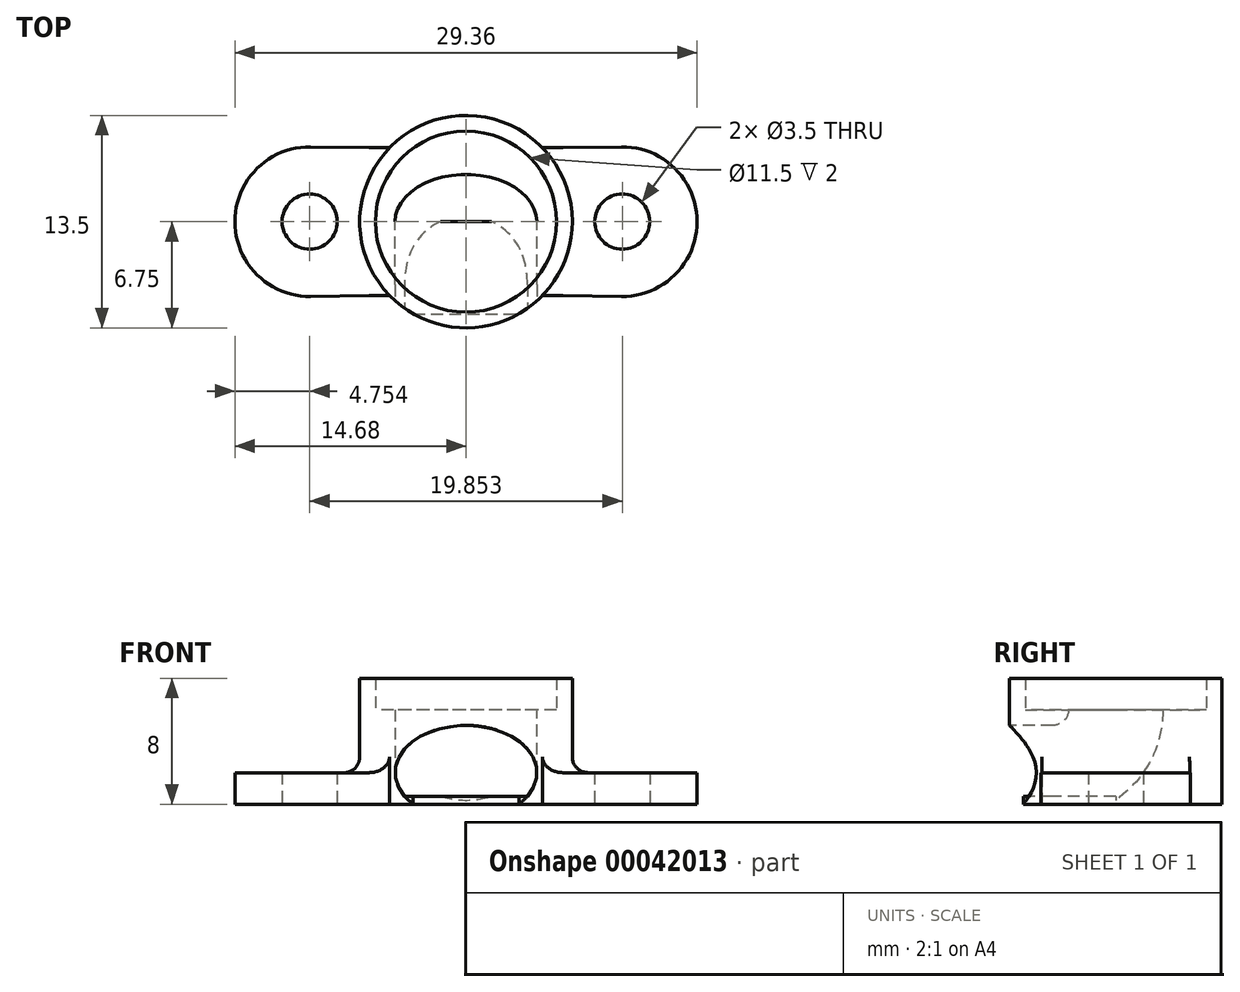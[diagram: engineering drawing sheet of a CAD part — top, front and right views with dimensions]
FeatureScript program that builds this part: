
annotation { "Feature Type Name" : "Feature", "Feature Type Description" : "" }
export const myFeature = defineFeature(function(context is Context, id is Id, definition is map)
    precondition{}
    {
        {
            var Q0;
            Q0=qCreatedBy(makeId("Top.planeOp"),FACE);
            var sketch = newSketch(context, id + "F0", { "sketchPlane" : qUnion([Q0])});
            skCircle(sketch, "E0", {"center": v(0, 0) * mm, "radius": 6.75 * mm});
            skSolve(sketch);
        }
        {
            var Q0;
            Q0=qSketchRegion(id+"F0",true);
            extrude(context, id + "F1", {"entities" : qUnion([Q0]), "depth" : 6 * mm});
        }
        {
            var Q0;
            Q0=makeQuery(id+"F1.opExtrude","CAP_FACE",FACE,{"disambiguationData":[OSD([sQuery(id+"F0.wireOp",EDGE,"E0")])],"isStart":false});
            var sketch = newSketch(context, id + "F2", { "sketchPlane" : qUnion([Q0])});
            skCircle(sketch, "E1", {"center": v(0, 0) * mm, "radius": 5.75 * mm});
            skCircle(sketch, "E2", {"center": v(0, 0) * mm, "radius": 6.75 * mm});
            skSolve(sketch);
        }
        {
            var Q0;
            Q0=makeQuery(id+"F2.imprint","IMPRINT",FACE,{"disambiguationData":[TD([[makeQuery(id+"F2.imprint","IMPRINT",EDGE,{"derivedFrom":sQuery(id+"F2.wireOp",EDGE,"E1")}),-1.0]])]});
            extrude(context, id + "F3", {"entities" : qUnion([Q0]), "operationType" : NewBodyOperationType.ADD, "depth" : 2 * mm});
        }
        {
            var Q0;
            Q0=qCreatedBy(makeId("Top.planeOp"),FACE);
            var sketch = newSketch(context, id + "F4", { "sketchPlane" : qUnion([Q0])});
            skArc(sketch, "E3", {"start": v(-9.87, 4.75) * mm, "mid": v(-14.68, 0) * mm, "end": v(-9.87, -4.75) * mm});
            skLineSegment(sketch, "E4", {"start": v(0, 5.94) * mm, "end": v(0, -6.04) * mm, "construction": true});
            skCircle(sketch, "E5", {"center": v(-9.93, 0) * mm, "radius": 1.75 * mm});
            skArc(sketch, "E6.MirrorCS", {"start": v(9.87, 4.75) * mm, "mid": v(14.68, 0) * mm, "end": v(9.87, -4.75) * mm});
            skCircle(sketch, "E7.MirrorC", {"center": v(9.93, 0) * mm, "radius": 1.75 * mm});
            skLineSegment(sketch, "E8", {"start": v(-5.5, 0) * mm, "end": v(5.77, 0) * mm, "construction": true});
            skLineSegment(sketch, "E9", {"start": v(-9.87, 4.75) * mm, "end": v(-4.85, 4.7) * mm});
            skLineSegment(sketch, "E10", {"start": v(-9.87, -4.75) * mm, "end": v(-4.85, -4.7) * mm});
            skLineSegment(sketch, "E11", {"start": v(9.87, -4.75) * mm, "end": v(4.85, -4.7) * mm});
            skLineSegment(sketch, "E12", {"start": v(9.87, 4.75) * mm, "end": v(4.85, 4.7) * mm});
            skFitSpline(sketch, "E13", {"points": [v(-4.85, -4.7) * mm, v(-4.85, -4.1) * mm, v(-5.7, -2.48) * mm, v(-6.17, 0) * mm, v(-5.5, 2.99) * mm, v(-4.85, 4.7) * mm], "startDerivative": vector(0.89, 4.78) * mm, "endDerivative": vector(3.16, 7.84) * mm});
            skFitSpline(sketch, "E14", {"points": [v(4.85, 4.7) * mm, v(5.63, 2.47) * mm, v(6.24, -0.23) * mm, v(5.72, -2.67) * mm, v(4.85, -4.7) * mm], "startDerivative": vector(3.1, -8.78) * mm, "endDerivative": vector(-3.8, -8.27) * mm});
            skSolve(sketch);
        }
        {
            var Q0;
            Q0=qSketchRegion(id+"F4",true);
            extrude(context, id + "F5", {"entities" : qUnion([Q0]), "operationType" : NewBodyOperationType.ADD, "depth" : 2 * mm});
        }
        {
            var Q0;
            Q0=makeQuery(id+"F5.boolean.opBoolean","INTERSECT",EDGE,{"derivedFrom":[makeQuery(id+"F3.boolean.opBoolean","MERGE",FACE,{"derivedFrom":[makeQuery(id+"F1.opExtrude","SWEPT_FACE",FACE,{"disambiguationData":[OSD([sQuery(id+"F0.wireOp",EDGE,"E0")])]}),makeQuery(id+"F3.opExtrude","SWEPT_FACE",FACE,{"disambiguationData":[OSD([sQuery(id+"F2.wireOp",EDGE,"E2")])]})]}),makeQuery(id+"F5.opExtrude","CAP_FACE",FACE,{"disambiguationData":[OSD([sQuery(id+"F4.wireOp",EDGE,"E6.MirrorCS"),sQuery(id+"F4.wireOp",EDGE,"E7.MirrorC"),sQuery(id+"F4.wireOp",EDGE,"E11"),sQuery(id+"F4.wireOp",EDGE,"E12"),sQuery(id+"F4.wireOp",EDGE,"E14")])],"isStart":false})]});
            var Q1;
            Q1=makeQuery(id+"F5.opExtrude","SWEPT_EDGE",EDGE,{"disambiguationData":[OSD([sQuery(id+"F4.wireOp",EDGE,"E11"),sQuery(id+"F4.wireOp",EDGE,"E14")])]});
            var Q2;
            Q2=makeQuery(id+"F5.opExtrude","SWEPT_EDGE",EDGE,{"disambiguationData":[OSD([sQuery(id+"F4.wireOp",EDGE,"E12"),sQuery(id+"F4.wireOp",EDGE,"E14")])]});
            var Q3;
            Q3=makeQuery(id+"F5.opExtrude","SWEPT_EDGE",EDGE,{"disambiguationData":[OSD([sQuery(id+"F4.wireOp",EDGE,"E9"),sQuery(id+"F4.wireOp",EDGE,"E13")])]});
            var Q4;
            Q4=makeQuery(id+"F5.boolean.opBoolean","INTERSECT",EDGE,{"derivedFrom":[makeQuery(id+"F3.boolean.opBoolean","MERGE",FACE,{"derivedFrom":[makeQuery(id+"F1.opExtrude","SWEPT_FACE",FACE,{"disambiguationData":[OSD([sQuery(id+"F0.wireOp",EDGE,"E0")])]}),makeQuery(id+"F3.opExtrude","SWEPT_FACE",FACE,{"disambiguationData":[OSD([sQuery(id+"F2.wireOp",EDGE,"E2")])]})]}),makeQuery(id+"F5.opExtrude","CAP_FACE",FACE,{"disambiguationData":[OSD([sQuery(id+"F4.wireOp",EDGE,"E3"),sQuery(id+"F4.wireOp",EDGE,"E5"),sQuery(id+"F4.wireOp",EDGE,"E9"),sQuery(id+"F4.wireOp",EDGE,"E10"),sQuery(id+"F4.wireOp",EDGE,"E13")])],"isStart":false})]});
            var Q5;
            Q5=makeQuery(id+"F5.opExtrude","SWEPT_EDGE",EDGE,{"disambiguationData":[OSD([sQuery(id+"F4.wireOp",EDGE,"E10"),sQuery(id+"F4.wireOp",EDGE,"E13")])]});
            fillet(context, id + "F6", {"entities" : qUnion([Q0, Q1, Q2, Q3, Q4, Q5]), "radius" : 1 * mm, "tangentPropagation" : true, "allowEdgeOverflow" : false});
        }
        {
            var Q0;
            Q0=makeQuery(id+"F1.opExtrude","CAP_FACE",FACE,{"disambiguationData":[OSD([sQuery(id+"F0.wireOp",EDGE,"E0")])],"isStart":false});
            var sketch = newSketch(context, id + "F7", { "sketchPlane" : qUnion([Q0])});
            skEllipse(sketch, "E15", {"center": v(0, 0) * mm, "majorRadius": 4.5 * mm, "minorRadius": 3 * mm, "majorAxis": v(1, 0)});
            skSolve(sketch);
        }
        {
            var Q0;
            Q0=qCreatedBy(makeId("Right.planeOp"),FACE);
            var sketch = newSketch(context, id + "F8", { "sketchPlane" : qUnion([Q0])});
            skLineSegment(sketch, "E16", {"start": v(0, 6) * mm, "end": v(0, 6) * mm});
            skLineSegment(sketch, "E17", {"start": v(-4, 2) * mm, "end": v(-9.96, 2) * mm});
            skPoint(sketch, "E18.visualSharp", {"position": v(0, 2) * mm});
            skArc(sketch, "E18.filletArc", {"start": v(-4, 2) * mm, "mid": v(-1.17, 3.17) * mm, "end": v(0, 6) * mm});
            skSolve(sketch);
        }
        {
            var Q0;
            Q0=qSketchRegion(id+"F7",true);
            var Q1;
            Q1=qConstructionFilter(qBodyType(qCreatedBy(id+"F8",EDGE),BodyType.WIRE),ConstructionObject.NO);
            sweep(context, id + "F9", {"operationType" : NewBodyOperationType.REMOVE, "profiles" : qUnion([Q0]), "path" : qUnion([Q1])});
        }
        {
            var Q0;
            Q0=makeQuery(id+"F5.boolean.opBoolean","MERGE",FACE,{"derivedFrom":[makeQuery(id+"F1.opExtrude","CAP_FACE",FACE,{"disambiguationData":[OSD([sQuery(id+"F0.wireOp",EDGE,"E0")])],"isStart":true}),makeQuery(id+"F5.opExtrude","CAP_FACE",FACE,{"disambiguationData":[OSD([sQuery(id+"F4.wireOp",EDGE,"E3"),sQuery(id+"F4.wireOp",EDGE,"E5"),sQuery(id+"F4.wireOp",EDGE,"E9"),sQuery(id+"F4.wireOp",EDGE,"E10"),sQuery(id+"F4.wireOp",EDGE,"E13")])],"isStart":true}),makeQuery(id+"F5.opExtrude","CAP_FACE",FACE,{"disambiguationData":[OSD([sQuery(id+"F4.wireOp",EDGE,"E6.MirrorCS"),sQuery(id+"F4.wireOp",EDGE,"E7.MirrorC"),sQuery(id+"F4.wireOp",EDGE,"E11"),sQuery(id+"F4.wireOp",EDGE,"E12"),sQuery(id+"F4.wireOp",EDGE,"E14")])],"isStart":true})]});
            var sketch = newSketch(context, id + "F10", { "sketchPlane" : qUnion([Q0])});
            skLineSegment(sketch, "E19.bottom", {"start": v(-4, 0) * mm, "end": v(4, 0) * mm});
            skLineSegment(sketch, "E19.left", {"start": v(-4, 0) * mm, "end": v(-4, 5.44) * mm});
            skLineSegment(sketch, "E19.right", {"start": v(4, 0) * mm, "end": v(4, 5.44) * mm});
            skLineSegment(sketch, "E20", {"start": v(-4, 5.44) * mm, "end": v(-3.35, 5.86) * mm});
            skLineSegment(sketch, "E21", {"start": v(-3.35, 5.86) * mm, "end": v(3.35, 5.86) * mm});
            skLineSegment(sketch, "E22", {"start": v(3.35, 5.86) * mm, "end": v(4, 5.44) * mm});
            skSolve(sketch);
        }
        {
            var Q0;
            Q0=qSketchRegion(id+"F10",true);
            extrude(context, id + "F11", {"entities" : qUnion([Q0]), "operationType" : NewBodyOperationType.ADD, "oppositeDirection" : true, "depth" : .5 * mm});
        }
    });
